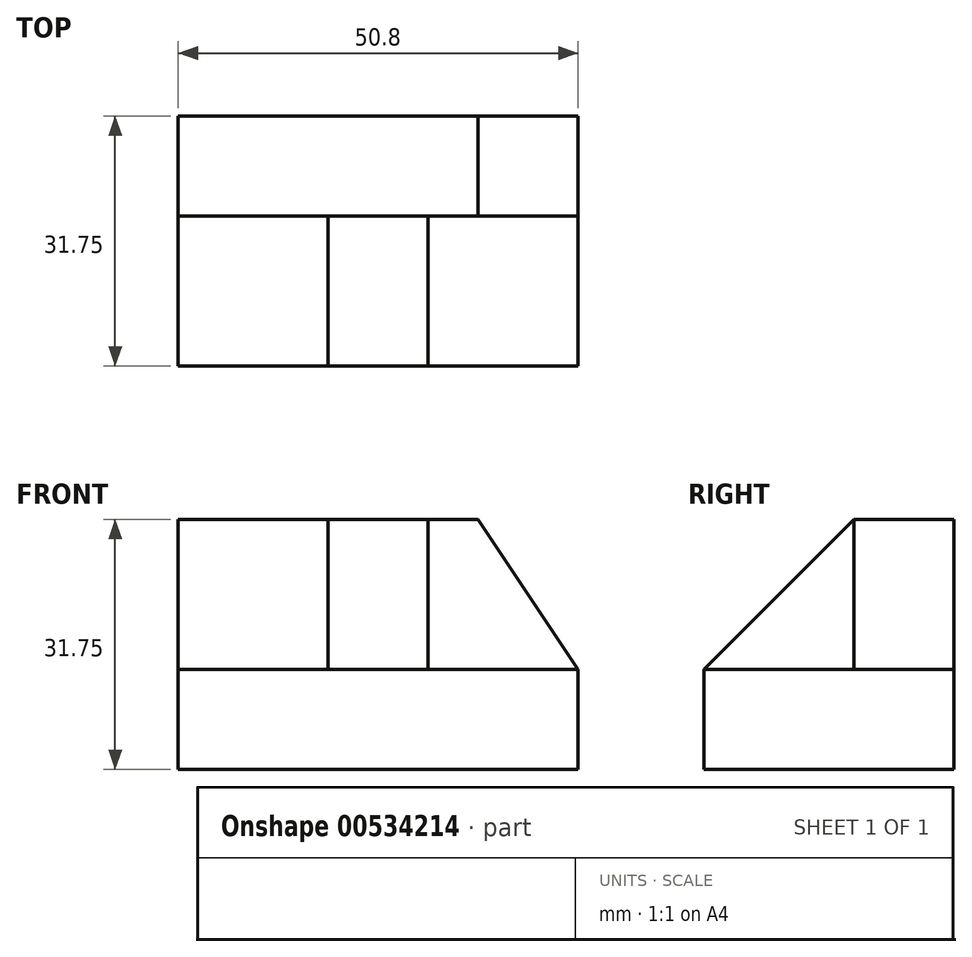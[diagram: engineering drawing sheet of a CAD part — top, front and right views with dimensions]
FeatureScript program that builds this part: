
annotation { "Feature Type Name" : "Feature", "Feature Type Description" : "" }
export const myFeature = defineFeature(function(context is Context, id is Id, definition is map)
    precondition{}
    {
        {
            var Q0;
            Q0=qCreatedBy(makeId("Right.planeOp"),FACE);
            var sketch = newSketch(context, id + "F0", { "sketchPlane" : qUnion([Q0])});
            skLineSegment(sketch, "E0", {"start": v(0, 0) * mm, "end": v(31.75, 0) * mm});
            skLineSegment(sketch, "E1", {"start": v(31.75, 0) * mm, "end": v(31.75, 31.75) * mm});
            skLineSegment(sketch, "E2", {"start": v(31.75, 31.75) * mm, "end": v(19.05, 31.75) * mm});
            skLineSegment(sketch, "E3", {"start": v(19.05, 31.75) * mm, "end": v(0, 12.7) * mm});
            skLineSegment(sketch, "E4", {"start": v(0, 12.7) * mm, "end": v(0, 0) * mm});
            skSolve(sketch);
        }
        {
            var Q0;
            Q0=makeQuery(id+"F0.imprint","IMPRINT",FACE,{"disambiguationData":[TD([[makeQuery(id+"F0.imprint","IMPRINT",EDGE,{"derivedFrom":sQuery(id+"F0.wireOp",EDGE,"E0")}),1.0]])]});
            extrude(context, id + "F1", {"entities" : qUnion([Q0]), "depth" : 50.8 * mm, "offsetDistance" : 25.4 * mm});
        }
        {
            var Q0;
            Q0=makeQuery(id+"F1.opExtrude","CAP_FACE",FACE,{"disambiguationData":[OSD([sQuery(id+"F0.wireOp",EDGE,"E0"),sQuery(id+"F0.wireOp",EDGE,"E1"),sQuery(id+"F0.wireOp",EDGE,"E2"),sQuery(id+"F0.wireOp",EDGE,"E3"),sQuery(id+"F0.wireOp",EDGE,"E4")])],"isStart":false});
            var sketch = newSketch(context, id + "F2", { "sketchPlane" : qUnion([Q0])});
            skLineSegment(sketch, "E5", {"start": v(19.05, 31.75) * mm, "end": v(19.05, 12.7) * mm});
            skLineSegment(sketch, "E6", {"start": v(19.05, 12.7) * mm, "end": v(0, 12.7) * mm});
            skSolve(sketch);
        }
        {
            var Q0;
            Q0=makeQuery(id+"F2.imprint","IMPRINT",FACE,{"disambiguationData":[TD([[makeQuery(id+"F2.imprint","IMPRINT",EDGE,{"derivedFrom":sQuery(id+"F2.wireOp",EDGE,"E5")}),-1.0]])]});
            extrude(context, id + "F3", {"entities" : qUnion([Q0]), "operationType" : NewBodyOperationType.REMOVE, "oppositeDirection" : true, "depth" : 19.05 * mm, "offsetDistance" : 25.4 * mm});
        }
        {
            var Q0;
            Q0=makeQuery(id+"F1.opExtrude","CAP_FACE",FACE,{"disambiguationData":[OSD([sQuery(id+"F0.wireOp",EDGE,"E0"),sQuery(id+"F0.wireOp",EDGE,"E1"),sQuery(id+"F0.wireOp",EDGE,"E2"),sQuery(id+"F0.wireOp",EDGE,"E3"),sQuery(id+"F0.wireOp",EDGE,"E4")])],"isStart":true});
            var sketch = newSketch(context, id + "F4", { "sketchPlane" : qUnion([Q0])});
            skLineSegment(sketch, "E7", {"start": v(0, 12.7) * mm, "end": v(-19.05, 12.7) * mm});
            skLineSegment(sketch, "E8", {"start": v(-19.05, 12.7) * mm, "end": v(-19.05, 31.75) * mm});
            skSolve(sketch);
        }
        {
            var Q0;
            Q0=makeQuery(id+"F4.imprint","IMPRINT",FACE,{"disambiguationData":[TD([[makeQuery(id+"F4.imprint","IMPRINT",EDGE,{"derivedFrom":sQuery(id+"F4.wireOp",EDGE,"E7")}),-1.0]])]});
            extrude(context, id + "F5", {"entities" : qUnion([Q0]), "operationType" : NewBodyOperationType.REMOVE, "oppositeDirection" : true, "depth" : 19.05 * mm, "offsetDistance" : 25.4 * mm});
        }
        {
            var Q0;
            Q0=makeQuery(id+"F3.boolean.opBoolean","COPY",FACE,{"derivedFrom":makeQuery(id+"F3.opExtrude","SWEPT_FACE",FACE,{"disambiguationData":[OSD([sQuery(id+"F2.wireOp",EDGE,"E5")])]})});
            var sketch = newSketch(context, id + "F6", { "sketchPlane" : qUnion([Q0])});
            skLineSegment(sketch, "E9", {"start": v(38.1, 31.75) * mm, "end": v(50.8, 12.7) * mm});
            skLineSegment(sketch, "E10", {"start": v(50.8, 12.7) * mm, "end": v(50.8, 31.75) * mm});
            skLineSegment(sketch, "E11", {"start": v(50.8, 31.75) * mm, "end": v(38.1, 31.75) * mm});
            skSolve(sketch);
        }
        {
            var Q0;
            Q0=makeQuery(id+"F6.imprint","IMPRINT",FACE,{"disambiguationData":[TD([[makeQuery(id+"F6.imprint","IMPRINT",EDGE,{"derivedFrom":sQuery(id+"F6.wireOp",EDGE,"E9")}),1.0]])]});
            extrude(context, id + "F7", {"entities" : qUnion([Q0]), "operationType" : NewBodyOperationType.REMOVE, "oppositeDirection" : true, "depth" : 12.7 * mm, "offsetDistance" : 25.4 * mm});
        }
    });
